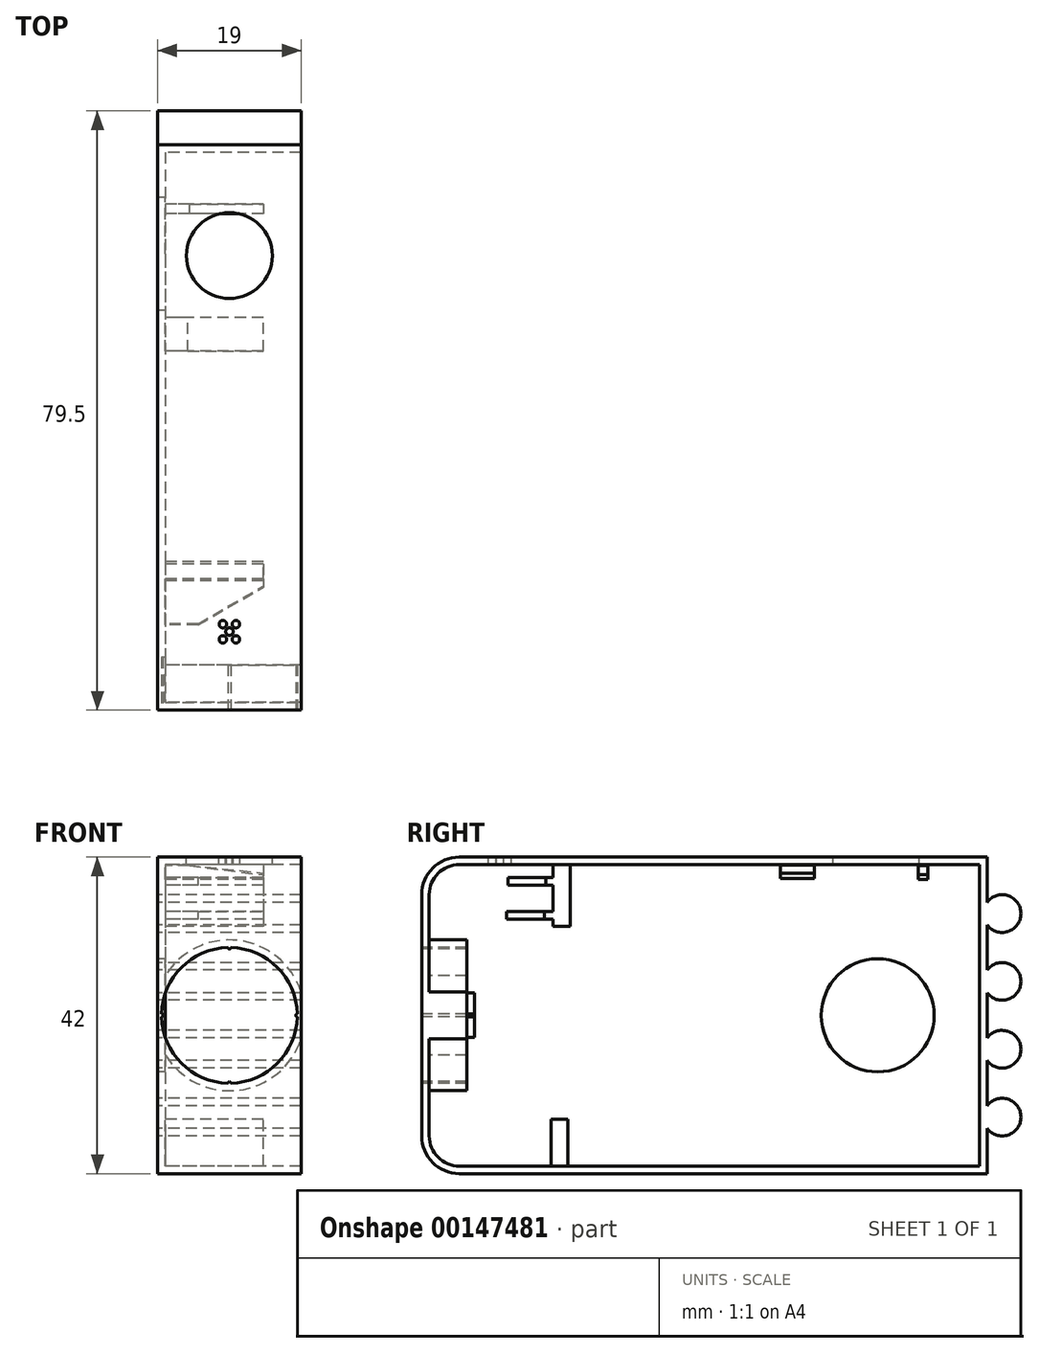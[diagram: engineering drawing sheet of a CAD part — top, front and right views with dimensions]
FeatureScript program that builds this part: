
annotation { "Feature Type Name" : "Feature", "Feature Type Description" : "" }
export const myFeature = defineFeature(function(context is Context, id is Id, definition is map)
    precondition{}
    {
        {
            var Q0;
            Q0=qCreatedBy(makeId("Top.planeOp"),FACE);
            var sketch = newSketch(context, id + "F0", { "sketchPlane" : qUnion([Q0])});
            skLineSegment(sketch, "E0.bottom", {"start": v(9.5, 37.5) * mm, "end": v(-9.5, 37.5) * mm});
            skLineSegment(sketch, "E0.top", {"start": v(9.5, -37.5) * mm, "end": v(-9.5, -37.5) * mm});
            skLineSegment(sketch, "E0.left", {"start": v(9.5, 37.5) * mm, "end": v(9.5, -37.5) * mm});
            skLineSegment(sketch, "E0.right", {"start": v(-9.5, 37.5) * mm, "end": v(-9.5, -37.5) * mm});
            skPoint(sketch, "E0.middle", {"position": v(0, 0) * mm});
            skSolve(sketch);
        }
        {
            var Q0;
            Q0 = qSketchRegion(id + "F0", true);
            extrude(context, id + "F1", {"entities" : qUnion([Q0]), "depth" : 42 * mm});
        }
        {
            var Q0;
            Q0=makeQuery(id+"F1.opExtrude","SWEPT_FACE",FACE,{"disambiguationData":[OSD([sQuery(id+"F0.wireOp",EDGE,"E0.top")])]});
            var sketch = newSketch(context, id + "F2", { "sketchPlane" : qUnion([Q0])});
            skLineSegment(sketch, "E1", {"start": v(0, 53.77) * mm, "end": v(0, 30.2) * mm, "construction": true});
            skLineSegment(sketch, "E2", {"start": v(-22.42, 21) * mm, "end": v(28.87, 21) * mm, "construction": true});
            skPoint(sketch, "E2.startSnap0", {"position": v(0, 21) * mm});
            skArc(sketch, "E3", {"start": v(-0.2, 30) * mm, "mid": v(-6.36, 27.36) * mm, "end": v(-9, 21.2) * mm});
            skArc(sketch, "E4", {"start": v(-0.2, 30) * mm, "mid": v(0, 29.8) * mm, "end": v(0.2, 30) * mm});
            skArc(sketch, "E5.1.0", {"start": v(-9, 20.8) * mm, "mid": v(-8.8, 21) * mm, "end": v(-9, 21.2) * mm});
            skArc(sketch, "E5.2.0", {"start": v(0.2, 12) * mm, "mid": v(0, 12.2) * mm, "end": v(-0.2, 12) * mm});
            skArc(sketch, "E5.3.0", {"start": v(9, 21.2) * mm, "mid": v(8.8, 21) * mm, "end": v(9, 20.8) * mm});
            skLineSegment(sketch, "E6.trimOffspring", {"start": v(0, 30) * mm, "end": v(0, -11.77) * mm, "construction": true});
            skArc(sketch, "E7.trimOffspring", {"start": v(-9, 20.8) * mm, "mid": v(-6.36, 14.64) * mm, "end": v(-0.2, 12) * mm});
            skArc(sketch, "E8.trimOffspring", {"start": v(9, 21.2) * mm, "mid": v(6.36, 27.36) * mm, "end": v(0.2, 30) * mm});
            skArc(sketch, "E9.trimOffspring", {"start": v(0.2, 12) * mm, "mid": v(6.36, 14.64) * mm, "end": v(9, 20.8) * mm});
            skSolve(sketch);
        }
        {
            var Q0;
            Q0=makeQuery(id+"F1.opExtrude","CAP_EDGE",EDGE,{"disambiguationData":[OSD([sQuery(id+"F0.wireOp",EDGE,"E0.top")])],"isStart":false});
            var Q1;
            Q1=makeQuery(id+"F1.opExtrude","CAP_EDGE",EDGE,{"disambiguationData":[OSD([sQuery(id+"F0.wireOp",EDGE,"E0.top")])],"isStart":true});
            fillet(context, id + "F3", {"entities" : qUnion([Q0, Q1]), "radius" : 5 * mm, "tangentPropagation" : true, "allowEdgeOverflow" : false});
        }
        {
            var Q0;
            Q0 = qSketchRegion(id + "F2", true);
            extrude(context, id + "F4", {"entities" : qUnion([Q0]), "operationType" : NewBodyOperationType.REMOVE, "oppositeDirection" : true, "depth" : 5 * mm});
        }
        {
            var Q0;
            Q0=makeQuery(id+"F1.opExtrude","SWEPT_FACE",FACE,{"disambiguationData":[OSD([sQuery(id+"F0.wireOp",EDGE,"E0.left")])]});
            shell(context, id + "F5", {"entities" : qUnion([Q0]), "thickness" : 1 * mm});
        }
        {
            var Q0;
            Q0=makeQuery(id+"F1.opExtrude","CAP_FACE",FACE,{"disambiguationData":[OSD([sQuery(id+"F0.wireOp",EDGE,"E0.bottom"),sQuery(id+"F0.wireOp",EDGE,"E0.top"),sQuery(id+"F0.wireOp",EDGE,"E0.left"),sQuery(id+"F0.wireOp",EDGE,"E0.right")])],"isStart":false});
            var sketch = newSketch(context, id + "F6", { "sketchPlane" : qUnion([Q0])});
            skCircle(sketch, "E10", {"center": v(0, 22.8) * mm, "radius": 5.7 * mm});
            skSolve(sketch);
        }
        {
            var Q0;
            Q0=makeQuery(id+"F1.opExtrude","SWEPT_FACE",FACE,{"disambiguationData":[OSD([sQuery(id+"F0.wireOp",EDGE,"E0.right")])]});
            var sketch = newSketch(context, id + "F7", { "sketchPlane" : qUnion([Q0])});
            skCircle(sketch, "E11", {"center": v(-23, 21) * mm, "radius": 7.5 * mm});
            skPoint(sketch, "E11.centerSnap0", {"position": v(-37.5, 21) * mm});
            skSolve(sketch);
        }
        {
            var Q0;
            Q0=makeQuery(id+"F6.imprint","IMPRINT",FACE,{"disambiguationData":[TD([[makeQuery(id+"F6.imprint","IMPRINT",EDGE,{"derivedFrom":sQuery(id+"F6.wireOp",EDGE,"E10")}),-1.0]])]});
            var sketch = newSketch(context, id + "F8", { "sketchPlane" : qUnion([Q0])});
            skCircle(sketch, "E12", {"center": v(0, -27.09) * mm, "radius": 0.5 * mm});
            skCircle(sketch, "E13", {"center": v(0.86, -26.1) * mm, "radius": 0.5 * mm});
            skCircle(sketch, "E14", {"center": v(0.86, -28.12) * mm, "radius": 0.5 * mm});
            skCircle(sketch, "E15", {"center": v(-0.87, -28.12) * mm, "radius": 0.5 * mm});
            skCircle(sketch, "E16", {"center": v(-0.87, -26.1) * mm, "radius": 0.5 * mm});
            skSolve(sketch);
        }
        {
            var Q0;
            Q0 = qSketchRegion(id + "F8", true);
            extrude(context, id + "F9", {"entities" : qUnion([Q0]), "operationType" : NewBodyOperationType.REMOVE, "oppositeDirection" : true, "depth" : 10 * mm});
        }
        {
            var Q0;
            Q0 = qSketchRegion(id + "F6", true);
            extrude(context, id + "F10", {"entities" : qUnion([Q0]), "operationType" : NewBodyOperationType.REMOVE, "oppositeDirection" : true, "depth" : 25 * mm});
        }
        {
            var Q0;
            Q0 = qSketchRegion(id + "F7", true);
            extrude(context, id + "F11", {"entities" : qUnion([Q0]), "operationType" : NewBodyOperationType.REMOVE, "oppositeDirection" : true, "depth" : 7.5 * mm});
        }
        {
            var Q0;
            Q0=qCreatedBy(makeId("Right.planeOp"),FACE);
            var sketch = newSketch(context, id + "F12", { "sketchPlane" : qUnion([Q0])});
            skCircle(sketch, "E17", {"center": v(39.5, 34.5) * mm, "radius": 2.5 * mm});
            skCircle(sketch, "E18.0.1.0", {"center": v(39.5, 25.5) * mm, "radius": 2.5 * mm});
            skCircle(sketch, "E18.0.2.0", {"center": v(39.5, 16.5) * mm, "radius": 2.5 * mm});
            skCircle(sketch, "E18.0.3.0", {"center": v(39.5, 7.5) * mm, "radius": 2.5 * mm});
            skLineSegment(sketch, "E18.direction1", {"start": v(39.5, 34.5) * mm, "end": v(62.98, 34.5) * mm, "construction": true});
            skLineSegment(sketch, "E18.direction2", {"start": v(39.5, 34.5) * mm, "end": v(39.5, 25.5) * mm, "construction": true});
            skSolve(sketch);
        }
        {
            var Q0;
            Q0 = qSketchRegion(id + "F12", true);
            var Q1;
            Q1=makeQuery(id+"F1.opExtrude","SWEPT_FACE",FACE,{"disambiguationData":[OSD([sQuery(id+"F0.wireOp",EDGE,"E0.left")])]});
            var Q2;
            Q2=makeQuery(id+"F1.opExtrude","SWEPT_FACE",FACE,{"disambiguationData":[OSD([sQuery(id+"F0.wireOp",EDGE,"E0.right")])]});
            extrude(context, id + "F13", {"entities" : qUnion([Q0]), "operationType" : NewBodyOperationType.ADD, "endBound" : BoundingType.UP_TO_SURFACE, "endBoundEntityFace" : qUnion([Q1]), "depth" : 25 * mm, "hasSecondDirection" : true, "secondDirectionBound" : SecondDirectionBoundingType.UP_TO_SURFACE, "secondDirectionOppositeDirection" : true, "secondDirectionBoundEntityFace" : qUnion([Q2]), "secondDirectionDepth" : 25 * mm});
        }
        {
            var Q0;
            Q0=makeQuery(id+"F5.opShell","OFFSET_FACE",FACE,{"disambiguationData":[OSD([sQuery(id+"F0.wireOp",EDGE,"E0.right")])]});
            var sketch = newSketch(context, id + "F14", { "sketchPlane" : qUnion([Q0])});
            skLineSegment(sketch, "E19.bottom", {"start": v(35.88, 40.75) * mm, "end": v(29.88, 40.75) * mm, "construction": true});
            skLineSegment(sketch, "E19.top", {"start": v(35.88, 1.25) * mm, "end": v(30.88, 1.25) * mm, "construction": true});
            skLineSegment(sketch, "E19.left", {"start": v(35.88, 40.75) * mm, "end": v(35.88, 1.25) * mm, "construction": true});
            skLineSegment(sketch, "E19.right", {"start": v(-17.12, 40.75) * mm, "end": v(-17.12, 1.25) * mm, "construction": true});
            skPoint(sketch, "E19.middle", {"position": v(9.38, 21) * mm});
            skCircle(sketch, "E20", {"center": v(22.88, 21) * mm, "radius": 9 * mm, "construction": true});
            skLineSegment(sketch, "E21", {"start": v(29.88, 40.75) * mm, "end": v(29.88, 38.83) * mm, "construction": true});
            skLineSegment(sketch, "E22", {"start": v(29.88, 38.83) * mm, "end": v(9.88, 38.83) * mm, "construction": true});
            skLineSegment(sketch, "E23", {"start": v(9.88, 38.83) * mm, "end": v(9.88, 40.75) * mm, "construction": true});
            skLineSegment(sketch, "E24", {"start": v(30.88, 1.25) * mm, "end": v(30.88, 3.25) * mm, "construction": true});
            skLineSegment(sketch, "E25", {"start": v(30.88, 3.25) * mm, "end": v(23.88, 3.25) * mm, "construction": true});
            skLineSegment(sketch, "E26", {"start": v(23.88, 3.25) * mm, "end": v(23.88, 1.25) * mm, "construction": true});
            skLineSegment(sketch, "E27.trimOffspring", {"start": v(9.88, 40.75) * mm, "end": v(-17.12, 40.75) * mm, "construction": true});
            skLineSegment(sketch, "E28.trimOffspring", {"start": v(23.88, 1.25) * mm, "end": v(-17.12, 1.25) * mm, "construction": true});
            skLineSegment(sketch, "E29.bottom", {"start": v(10.1, 39.12) * mm, "end": v(14.56, 39.12) * mm});
            skLineSegment(sketch, "E29.top", {"start": v(10.1, 40.92) * mm, "end": v(14.56, 40.92) * mm});
            skLineSegment(sketch, "E29.left", {"start": v(10.1, 39.12) * mm, "end": v(10.1, 40.92) * mm});
            skLineSegment(sketch, "E29.right", {"start": v(14.56, 39.12) * mm, "end": v(14.56, 40.92) * mm});
            skLineSegment(sketch, "E30.bottom", {"start": v(29.65, 39.04) * mm, "end": v(28.35, 39.04) * mm});
            skLineSegment(sketch, "E30.top", {"start": v(29.65, 40.84) * mm, "end": v(28.35, 40.84) * mm});
            skLineSegment(sketch, "E30.left", {"start": v(29.65, 39.04) * mm, "end": v(29.65, 40.84) * mm});
            skLineSegment(sketch, "E30.right", {"start": v(28.35, 39.04) * mm, "end": v(28.35, 40.84) * mm});
            skLineSegment(sketch, "E31.bottom", {"start": v(-17.8, 41.2) * mm, "end": v(-20.1, 41.2) * mm});
            skLineSegment(sketch, "E31.top", {"start": v(-17.8, 32.81) * mm, "end": v(-20.1, 32.81) * mm});
            skLineSegment(sketch, "E31.left", {"start": v(-17.8, 41.2) * mm, "end": v(-17.8, 32.81) * mm});
            skLineSegment(sketch, "E31.right", {"start": v(-20.1, 41.2) * mm, "end": v(-20.1, 39.28) * mm});
            skLineSegment(sketch, "E32", {"start": v(-20.1, 39.28) * mm, "end": v(-26.04, 39.28) * mm});
            skLineSegment(sketch, "E33", {"start": v(-26.04, 39.28) * mm, "end": v(-26.04, 38.28) * mm});
            skLineSegment(sketch, "E34", {"start": v(-26.04, 38.28) * mm, "end": v(-20.1, 38.28) * mm});
            skLineSegment(sketch, "E35", {"start": v(-20.1, 38.28) * mm, "end": v(-20.1, 34.78) * mm});
            skLineSegment(sketch, "E36", {"start": v(-20.1, 34.78) * mm, "end": v(-26.21, 34.78) * mm});
            skLineSegment(sketch, "E37", {"start": v(-26.21, 34.78) * mm, "end": v(-26.21, 33.78) * mm});
            skLineSegment(sketch, "E38", {"start": v(-26.21, 33.78) * mm, "end": v(-20.1, 33.78) * mm});
            skLineSegment(sketch, "E39.trimOffspring", {"start": v(-20.1, 33.78) * mm, "end": v(-20.1, 32.81) * mm});
            skLineSegment(sketch, "E40.bottom", {"start": v(-18.1, 1) * mm, "end": v(-20.33, 1) * mm});
            skLineSegment(sketch, "E40.top", {"start": v(-18.1, 7.2) * mm, "end": v(-20.33, 7.2) * mm});
            skLineSegment(sketch, "E40.left", {"start": v(-18.1, 1) * mm, "end": v(-18.1, 7.2) * mm});
            skLineSegment(sketch, "E40.right", {"start": v(-20.33, 1) * mm, "end": v(-20.33, 7.2) * mm});
            skSolve(sketch);
        }
        {
            var Q0;
            Q0 = qSketchRegion(id + "F14", true);
            extrude(context, id + "F15", {"entities" : qUnion([Q0]), "operationType" : NewBodyOperationType.ADD, "depth" : 13 * mm});
        }
        {
            var Q0;
            Q0=makeQuery(id+"F15.opExtrude","CAP_EDGE",EDGE,{"disambiguationData":[OSD([sQuery(id+"F14.wireOp",EDGE,"E33")])],"isStart":false});
            var Q1;
            Q1=makeQuery(id+"F15.opExtrude","CAP_EDGE",EDGE,{"disambiguationData":[OSD([sQuery(id+"F14.wireOp",EDGE,"E37")])],"isStart":false});
            chamfer(context, id + "F16", {"entities" : qUnion([Q0, Q1]), "chamferType" : ChamferType.OFFSET_ANGLE, "width" : 5 * mm, "oppositeDirection" : false, "angle" : 60 * degree, "tangentPropagation" : true});
        }
        {
            var Q0;
            Q0=makeQuery(id+"F15.opExtrude","CAP_EDGE",EDGE,{"disambiguationData":[OSD([sQuery(id+"F14.wireOp",EDGE,"E29.top")])],"isStart":false});
            chamfer(context, id + "F17", {"entities" : qUnion([Q0]), "chamferType" : ChamferType.OFFSET_ANGLE, "width" : 10 * mm, "oppositeDirection" : false, "angle" : 6 * degree, "tangentPropagation" : true});
        }
        {
            var Q0;
            Q0=makeQuery(id+"F15.opExtrude","CAP_EDGE",EDGE,{"disambiguationData":[OSD([sQuery(id+"F14.wireOp",EDGE,"E30.top")])],"isStart":false});
            chamfer(context, id + "F18", {"entities" : qUnion([Q0]), "chamferType" : ChamferType.OFFSET_ANGLE, "width" : 1.2 * mm, "oppositeDirection" : false, "angle" : 83 * degree, "tangentPropagation" : true});
        }
        {
            var Q0;
            Q0=makeQuery(id+"F1.opExtrude","SWEPT_FACE",FACE,{"disambiguationData":[OSD([sQuery(id+"F0.wireOp",EDGE,"E0.top")])]});
            var sketch = newSketch(context, id + "F19", { "sketchPlane" : qUnion([Q0])});
            skLineSegment(sketch, "E41", {"start": v(0, 74.91) * mm, "end": v(0, 30.2) * mm, "construction": true});
            skLineSegment(sketch, "E42", {"start": v(-22.8, 21) * mm, "end": v(28.5, 21) * mm, "construction": true});
            skPoint(sketch, "E42.startSnap0", {"position": v(0, 21) * mm});
            skArc(sketch, "E43", {"start": v(-0.2, 30) * mm, "mid": v(-6.36, 27.36) * mm, "end": v(-9, 21.2) * mm});
            skArc(sketch, "E44", {"start": v(-0.2, 30) * mm, "mid": v(0, 29.8) * mm, "end": v(0.2, 30) * mm});
            skArc(sketch, "E45.1.0", {"start": v(-9, 20.8) * mm, "mid": v(-8.8, 21) * mm, "end": v(-9, 21.2) * mm});
            skArc(sketch, "E45.2.0", {"start": v(0.2, 12) * mm, "mid": v(0, 12.2) * mm, "end": v(-0.2, 12) * mm});
            skArc(sketch, "E45.3.0", {"start": v(9, 21.2) * mm, "mid": v(8.8, 21) * mm, "end": v(9, 20.8) * mm});
            skLineSegment(sketch, "E46.trimOffspring", {"start": v(0, 30) * mm, "end": v(0, -32.91) * mm, "construction": true});
            skArc(sketch, "E47.trimOffspring", {"start": v(-9, 20.8) * mm, "mid": v(-6.36, 14.64) * mm, "end": v(-0.2, 12) * mm});
            skArc(sketch, "E48.trimOffspring", {"start": v(9, 21.2) * mm, "mid": v(6.36, 27.36) * mm, "end": v(0.2, 30) * mm});
            skArc(sketch, "E49.trimOffspring", {"start": v(0.2, 12) * mm, "mid": v(6.36, 14.64) * mm, "end": v(9, 20.8) * mm});
            skSolve(sketch);
        }
        {
            var Q0;
            Q0 = qSketchRegion(id + "F19", true);
            extrude(context, id + "F20", {"entities" : qUnion([Q0]), "operationType" : NewBodyOperationType.REMOVE, "oppositeDirection" : true, "depth" : 7 * mm});
        }
    });
